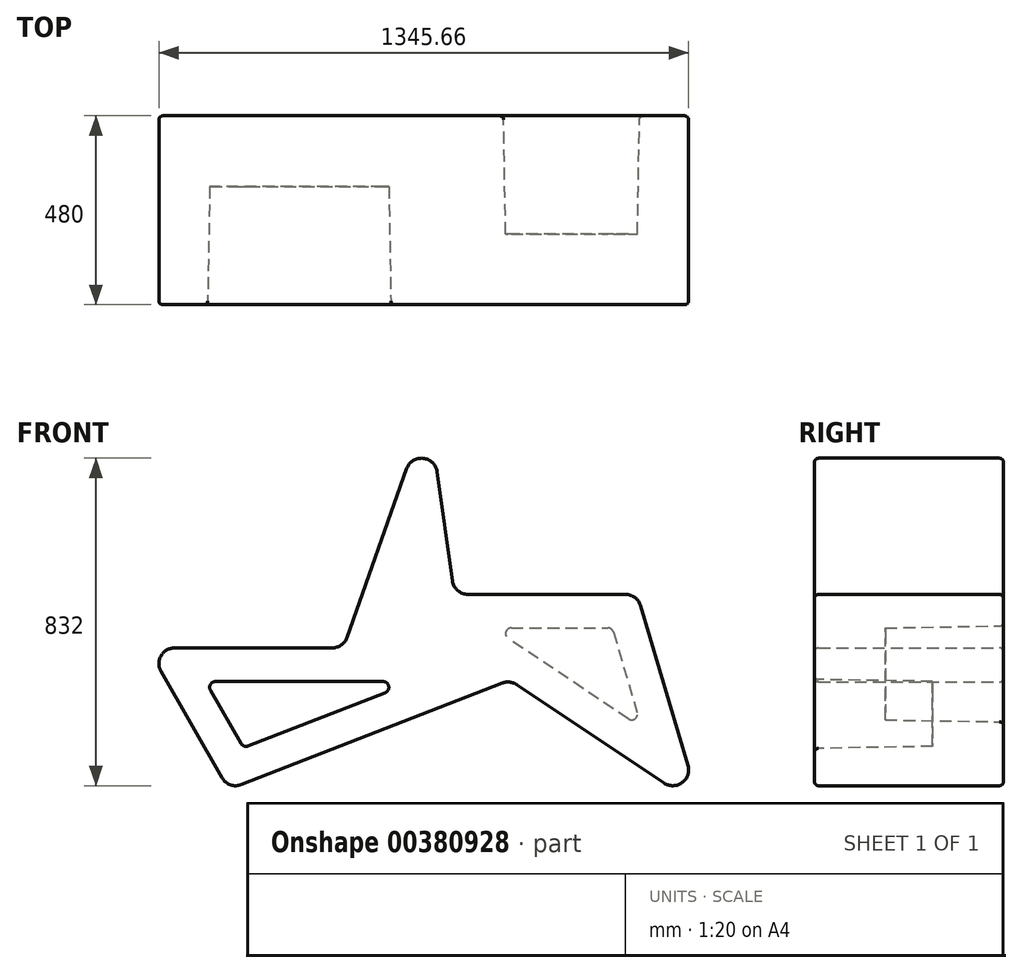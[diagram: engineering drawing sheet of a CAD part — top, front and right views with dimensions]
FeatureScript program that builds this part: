
annotation { "Feature Type Name" : "Feature", "Feature Type Description" : "" }
export const myFeature = defineFeature(function(context is Context, id is Id, definition is map)
    precondition{}
    {
        {
            var Q0;
            Q0=qCreatedBy(makeId("Front.planeOp"),FACE);
            var sketch = newSketch(context, id + "F0", { "sketchPlane" : qUnion([Q0])});
            skSolve(sketch);
        }
        {
            var Q0;
            Q0=qCreatedBy(makeId("Front.planeOp"),FACE);
            var sketch = newSketch(context, id + "F1", { "sketchPlane" : qUnion([Q0])});
            skLineSegment(sketch, "E0", {"start": v(-115.36, 350) * mm, "end": v(284.64, 350) * mm});
            skLineSegment(sketch, "E1", {"start": v(322.35, 376.65) * mm, "end": v(474.16, 805.35) * mm});
            skLineSegment(sketch, "E2", {"start": v(551.48, 797.57) * mm, "end": v(590.43, 520.43) * mm});
            skLineSegment(sketch, "E3", {"start": v(630.04, 486) * mm, "end": v(1030.04, 486) * mm});
            skLineSegment(sketch, "E4", {"start": v(1068.39, 457.36) * mm, "end": v(1188.65, 51.36) * mm});
            skLineSegment(sketch, "E5", {"start": v(1128.09, 6.73) * mm, "end": v(753.85, 256.63) * mm});
            skLineSegment(sketch, "E6", {"start": v(717.13, 260.64) * mm, "end": v(54.5, 2.72) * mm});
            skLineSegment(sketch, "E7", {"start": v(5.33, 20.05) * mm, "end": v(-150.03, 290.05) * mm});
            skPoint(sketch, "E8.visualSharp", {"position": v(528.73, 959.44) * mm});
            skArc(sketch, "E8.filletArc", {"start": v(551.48, 797.57) * mm, "mid": v(515.87, 831.8) * mm, "end": v(474.16, 805.35) * mm});
            skPoint(sketch, "E9.visualSharp", {"position": v(595.26, 486) * mm});
            skArc(sketch, "E9.filletArc", {"start": v(590.43, 520.43) * mm, "mid": v(603.8, 495.81) * mm, "end": v(630.04, 486) * mm});
            skPoint(sketch, "E10.visualSharp", {"position": v(312.91, 350) * mm});
            skArc(sketch, "E10.filletArc", {"start": v(284.64, 350) * mm, "mid": v(307.73, 357.33) * mm, "end": v(322.35, 376.65) * mm});
            skPoint(sketch, "E11.visualSharp", {"position": v(22.47, -9.74) * mm});
            skArc(sketch, "E11.filletArc", {"start": v(5.33, 20.05) * mm, "mid": v(26.7, 2.27) * mm, "end": v(54.5, 2.72) * mm});
            skPoint(sketch, "E12.visualSharp", {"position": v(736.53, 268.19) * mm});
            skArc(sketch, "E12.filletArc", {"start": v(753.85, 256.63) * mm, "mid": v(735.98, 263.12) * mm, "end": v(717.13, 260.64) * mm});
            skPoint(sketch, "E13.visualSharp", {"position": v(1220.06, -54.68) * mm});
            skArc(sketch, "E13.filletArc", {"start": v(1128.09, 6.73) * mm, "mid": v(1174.03, 7.8) * mm, "end": v(1188.65, 51.36) * mm});
            skPoint(sketch, "E14.visualSharp", {"position": v(1059.9, 486) * mm});
            skArc(sketch, "E14.filletArc", {"start": v(1068.39, 457.36) * mm, "mid": v(1053.97, 478.05) * mm, "end": v(1030.04, 486) * mm});
            skPoint(sketch, "E15.visualSharp", {"position": v(-184.52, 350) * mm});
            skArc(sketch, "E15.filletArc", {"start": v(-115.36, 350) * mm, "mid": v(-149.98, 330.03) * mm, "end": v(-150.03, 290.05) * mm});
            skLineSegment(sketch, "E16.bottom", {"start": v(0, 832) * mm, "end": v(1190.3, 832) * mm, "construction": true});
            skLineSegment(sketch, "E16.top", {"start": v(0, 0) * mm, "end": v(1190.3, 0) * mm, "construction": true});
            skLineSegment(sketch, "E16.left", {"start": v(0, 832) * mm, "end": v(0, 0) * mm, "construction": true});
            skLineSegment(sketch, "E16.right", {"start": v(1190.3, 832) * mm, "end": v(1190.3, 0) * mm, "construction": true});
            skLineSegment(sketch, "E17", {"start": v(520.63, 270) * mm, "end": v(57.53, 89.74) * mm, "construction": true});
            skLineSegment(sketch, "E18", {"start": v(57.53, 89.74) * mm, "end": v(-46.2, 270) * mm, "construction": true});
            skLineSegment(sketch, "E19", {"start": v(-46.2, 270) * mm, "end": v(520.63, 270) * mm, "construction": true});
            skLineSegment(sketch, "E20", {"start": v(176.13, 1064.28) * mm, "end": v(1406.01, 243.05) * mm, "construction": true});
            skLineSegment(sketch, "E21", {"start": v(1080.53, 134.68) * mm, "end": v(1000.17, 406) * mm, "construction": true});
            skLineSegment(sketch, "E22", {"start": v(1000.17, 406) * mm, "end": v(674.2, 406) * mm, "construction": true});
            skLineSegment(sketch, "E23", {"start": v(674.2, 406) * mm, "end": v(1080.53, 134.68) * mm, "construction": true});
            skSolve(sketch);
        }
        {
            var Q0;
            Q0 = qSketchRegion(id + "F1", true);
            extrude(context, id + "F2", {"entities" : qUnion([Q0]), "depth" : 480 * mm});
        }
        {
            var Q0;
            Q0=makeQuery(id+"F1.imprint","IMPRINT",FACE,{"disambiguationData":[TD([[makeQuery(id+"F1.imprint","IMPRINT",EDGE,{"derivedFrom":sQuery(id+"F1.wireOp",EDGE,"E0")}),-1.0]])]});
            var sketch = newSketch(context, id + "F3", { "sketchPlane" : qUnion([Q0])});
            skLineSegment(sketch, "E24.0", {"start": v(1064.83, 187.7) * mm, "end": v(1004.4, 391.68) * mm});
            skLineSegment(sketch, "E24.1", {"start": v(729.07, 369.37) * mm, "end": v(1034.55, 165.39) * mm});
            skLineSegment(sketch, "E24.2", {"start": v(985.23, 406) * mm, "end": v(740.18, 406) * mm});
            skPoint(sketch, "E25.visualSharp", {"position": v(1080.53, 134.68) * mm});
            skArc(sketch, "E25.filletArc", {"start": v(1034.55, 165.39) * mm, "mid": v(1057.52, 165.92) * mm, "end": v(1064.83, 187.7) * mm});
            skPoint(sketch, "E26.visualSharp", {"position": v(1000.17, 406) * mm});
            skArc(sketch, "E26.filletArc", {"start": v(1004.4, 391.68) * mm, "mid": v(997.2, 402.03) * mm, "end": v(985.23, 406) * mm});
            skPoint(sketch, "E27.visualSharp", {"position": v(674.2, 406) * mm});
            skArc(sketch, "E27.filletArc", {"start": v(740.18, 406) * mm, "mid": v(721.04, 391.8) * mm, "end": v(729.07, 369.37) * mm});
            skSolve(sketch);
        }
        {
            var Q0;
            Q0 = qSketchRegion(id + "F3", true);
            extrude(context, id + "F4", {"entities" : qUnion([Q0]), "operationType" : NewBodyOperationType.REMOVE, "depth" : 300 * mm, "offsetDistance" : 25 * mm, "hasDraft" : true, "draftAngle" : 1 * degree, "draftPullDirection" : true});
        }
        {
            var Q0;
            Q0=makeQuery(id+"F2.opExtrude","CAP_FACE",FACE,{"disambiguationData":[OSD([sQuery(id+"F1.wireOp",EDGE,"E0"),sQuery(id+"F1.wireOp",EDGE,"E1"),sQuery(id+"F1.wireOp",EDGE,"E2"),sQuery(id+"F1.wireOp",EDGE,"E3"),sQuery(id+"F1.wireOp",EDGE,"E4"),sQuery(id+"F1.wireOp",EDGE,"E5"),sQuery(id+"F1.wireOp",EDGE,"E6"),sQuery(id+"F1.wireOp",EDGE,"E7"),sQuery(id+"F1.wireOp",EDGE,"E8.filletArc"),sQuery(id+"F1.wireOp",EDGE,"E9.filletArc"),sQuery(id+"F1.wireOp",EDGE,"E10.filletArc"),sQuery(id+"F1.wireOp",EDGE,"E11.filletArc"),sQuery(id+"F1.wireOp",EDGE,"E12.filletArc"),sQuery(id+"F1.wireOp",EDGE,"E13.filletArc"),sQuery(id+"F1.wireOp",EDGE,"E14.filletArc"),sQuery(id+"F1.wireOp",EDGE,"E15.filletArc")])],"isStart":false});
            var sketch = newSketch(context, id + "F5", { "sketchPlane" : qUnion([Q0])});
            skLineSegment(sketch, "E28.0", {"start": v(-11.61, 270) * mm, "end": v(414.1, 270) * mm});
            skLineSegment(sketch, "E28.1", {"start": v(48.95, 104.64) * mm, "end": v(-28.95, 240.03) * mm});
            skLineSegment(sketch, "E28.2", {"start": v(421.36, 231.36) * mm, "end": v(73.54, 95.98) * mm});
            skPoint(sketch, "E29.visualSharp", {"position": v(-46.2, 270) * mm});
            skArc(sketch, "E29.filletArc", {"start": v(-11.61, 270) * mm, "mid": v(-28.92, 260.01) * mm, "end": v(-28.95, 240.03) * mm});
            skPoint(sketch, "E30.visualSharp", {"position": v(57.53, 89.74) * mm});
            skArc(sketch, "E30.filletArc", {"start": v(48.95, 104.64) * mm, "mid": v(59.64, 95.75) * mm, "end": v(73.54, 95.98) * mm});
            skPoint(sketch, "E31.visualSharp", {"position": v(520.63, 270) * mm});
            skArc(sketch, "E31.filletArc", {"start": v(421.36, 231.36) * mm, "mid": v(433.77, 253.7) * mm, "end": v(414.1, 270) * mm});
            skSolve(sketch);
        }
        {
            var Q0;
            Q0 = qSketchRegion(id + "F5", true);
            extrude(context, id + "F6", {"entities" : qUnion([Q0]), "operationType" : NewBodyOperationType.REMOVE, "oppositeDirection" : true, "depth" : 300 * mm, "offsetDistance" : 25 * mm, "hasDraft" : true, "draftAngle" : 1 * degree, "draftPullDirection" : true});
        }
        {
            var Q0;
            Q0=makeQuery(id+"F2.opExtrude","CAP_FACE",FACE,{"disambiguationData":[OSD([sQuery(id+"F1.wireOp",EDGE,"E0"),sQuery(id+"F1.wireOp",EDGE,"E1"),sQuery(id+"F1.wireOp",EDGE,"E2"),sQuery(id+"F1.wireOp",EDGE,"E3"),sQuery(id+"F1.wireOp",EDGE,"E4"),sQuery(id+"F1.wireOp",EDGE,"E5"),sQuery(id+"F1.wireOp",EDGE,"E6"),sQuery(id+"F1.wireOp",EDGE,"E7"),sQuery(id+"F1.wireOp",EDGE,"E8.filletArc"),sQuery(id+"F1.wireOp",EDGE,"E9.filletArc"),sQuery(id+"F1.wireOp",EDGE,"E10.filletArc"),sQuery(id+"F1.wireOp",EDGE,"E11.filletArc"),sQuery(id+"F1.wireOp",EDGE,"E12.filletArc"),sQuery(id+"F1.wireOp",EDGE,"E13.filletArc"),sQuery(id+"F1.wireOp",EDGE,"E14.filletArc"),sQuery(id+"F1.wireOp",EDGE,"E15.filletArc")])],"isStart":false});
            var Q1;
            Q1=makeQuery(id+"F2.opExtrude","CAP_FACE",FACE,{"disambiguationData":[OSD([sQuery(id+"F1.wireOp",EDGE,"E0"),sQuery(id+"F1.wireOp",EDGE,"E1"),sQuery(id+"F1.wireOp",EDGE,"E2"),sQuery(id+"F1.wireOp",EDGE,"E3"),sQuery(id+"F1.wireOp",EDGE,"E4"),sQuery(id+"F1.wireOp",EDGE,"E5"),sQuery(id+"F1.wireOp",EDGE,"E6"),sQuery(id+"F1.wireOp",EDGE,"E7"),sQuery(id+"F1.wireOp",EDGE,"E8.filletArc"),sQuery(id+"F1.wireOp",EDGE,"E9.filletArc"),sQuery(id+"F1.wireOp",EDGE,"E10.filletArc"),sQuery(id+"F1.wireOp",EDGE,"E11.filletArc"),sQuery(id+"F1.wireOp",EDGE,"E12.filletArc"),sQuery(id+"F1.wireOp",EDGE,"E13.filletArc"),sQuery(id+"F1.wireOp",EDGE,"E14.filletArc"),sQuery(id+"F1.wireOp",EDGE,"E15.filletArc")])],"isStart":true});
            fillet(context, id + "F7", {"entities" : qUnion([Q0, Q1]), "radius" : 10 * mm, "tangentPropagation" : true, "allowEdgeOverflow" : false});
        }
    });
